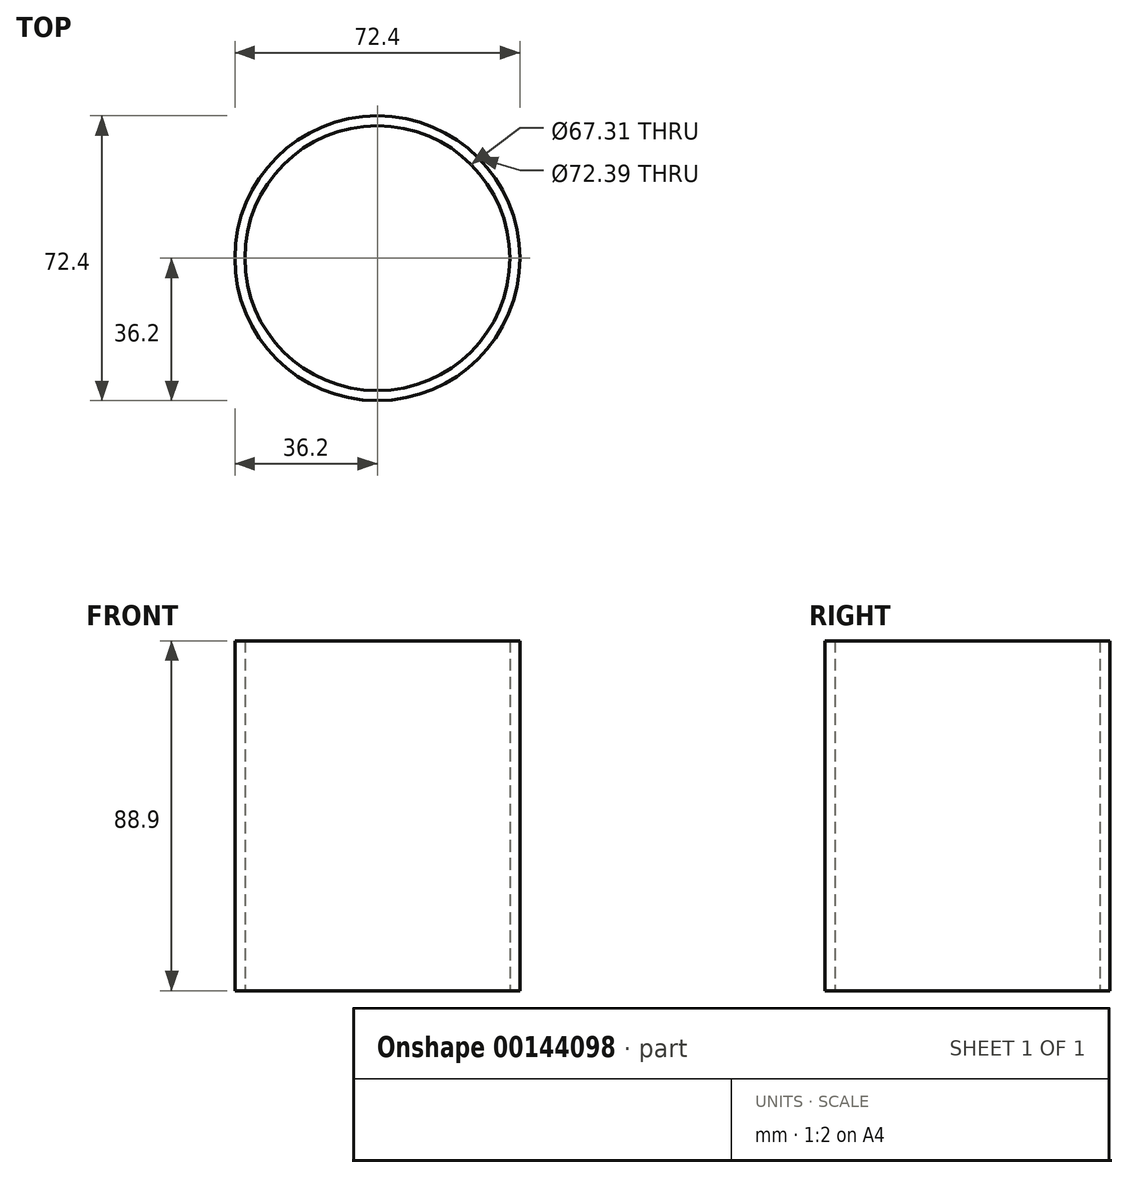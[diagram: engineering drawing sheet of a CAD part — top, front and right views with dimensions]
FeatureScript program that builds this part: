
annotation { "Feature Type Name" : "Feature", "Feature Type Description" : "" }
export const myFeature = defineFeature(function(context is Context, id is Id, definition is map)
    precondition{}
    {
        {
            var Q0;
            Q0=qCreatedBy(makeId("Top.planeOp"),FACE);
            var sketch = newSketch(context, id + "F0", { "sketchPlane" : qUnion([Q0])});
            skCircle(sketch, "E0", {"center": v(0, 0) * mm, "radius": 33.66 * mm});
            skCircle(sketch, "E1", {"center": v(0, 0) * mm, "radius": 36.2 * mm});
            skSolve(sketch);
        }
        {
            var Q0;
            Q0=sQuery(id+"F0.wireOp",EDGE,"E1");
            var Q1;
            Q1=sQuery(id+"F0.wireOp",EDGE,"E0");
            extrude(context, id + "F1", {"bodyType" : ToolBodyType.SURFACE, "surfaceEntities" : qUnion([Q0, Q1]), "oppositeDirection" : true, "depth" : 88.9 * mm});
        }
    });
